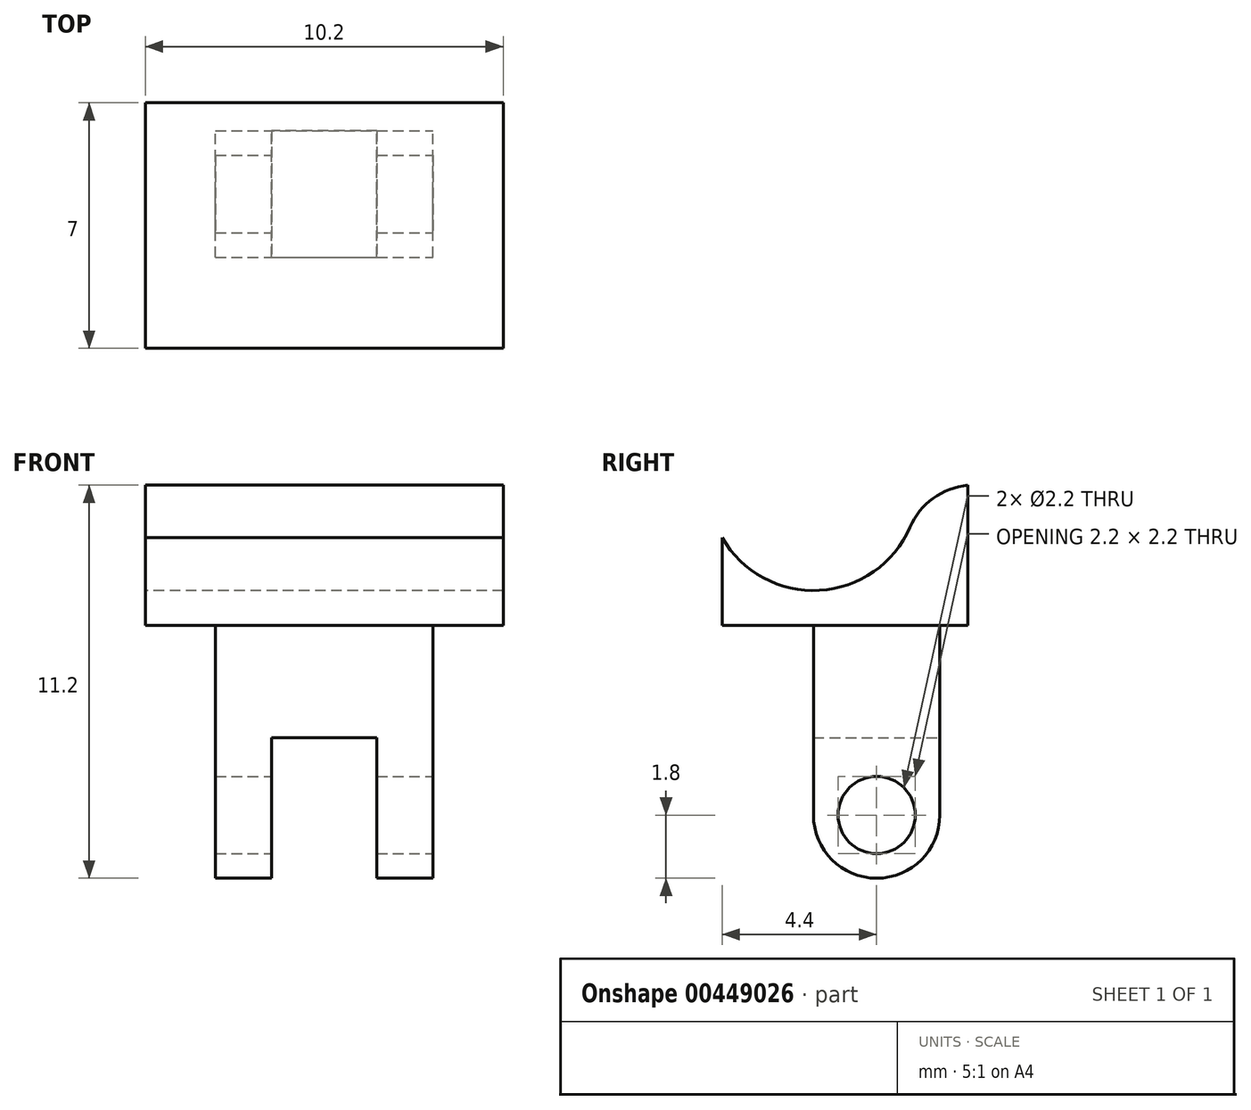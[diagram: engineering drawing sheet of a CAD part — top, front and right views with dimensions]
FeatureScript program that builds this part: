
annotation { "Feature Type Name" : "Feature", "Feature Type Description" : "" }
export const myFeature = defineFeature(function(context is Context, id is Id, definition is map)
    precondition{}
    {
        {
            var Q0;
            Q0=qCreatedBy(makeId("Top.planeOp"),FACE);
            var sketch = newSketch(context, id + "F0", { "sketchPlane" : qUnion([Q0])});
            skLineSegment(sketch, "E0.bottom", {"start": v(0, 0) * mm, "end": v(10.2, 0) * mm});
            skLineSegment(sketch, "E0.top", {"start": v(0, 7) * mm, "end": v(10.2, 7) * mm});
            skLineSegment(sketch, "E0.left", {"start": v(0, 0) * mm, "end": v(0, 7) * mm});
            skLineSegment(sketch, "E0.right", {"start": v(10.2, 0) * mm, "end": v(10.2, 7) * mm});
            skSolve(sketch);
        }
        {
            var Q0;
            Q0 = qSketchRegion(id + "F0", true);
            extrude(context, id + "F1", {"entities" : qUnion([Q0]), "depth" : 4 * mm});
        }
        {
            var Q0;
            Q0=makeQuery(id+"F1.opExtrude","CAP_FACE",FACE,{"disambiguationData":[OSD([sQuery(id+"F0.wireOp",EDGE,"E0.bottom"),sQuery(id+"F0.wireOp",EDGE,"E0.top"),sQuery(id+"F0.wireOp",EDGE,"E0.left"),sQuery(id+"F0.wireOp",EDGE,"E0.right")])],"isStart":true});
            var sketch = newSketch(context, id + "F2", { "sketchPlane" : qUnion([Q0])});
            skLineSegment(sketch, "E1.bottom", {"start": v(2, -2.6) * mm, "end": v(8.2, -2.6) * mm});
            skLineSegment(sketch, "E1.top", {"start": v(2, -6.2) * mm, "end": v(8.2, -6.2) * mm});
            skLineSegment(sketch, "E1.left", {"start": v(2, -2.6) * mm, "end": v(2, -6.2) * mm});
            skLineSegment(sketch, "E1.right", {"start": v(8.2, -2.6) * mm, "end": v(8.2, -6.2) * mm});
            skSolve(sketch);
        }
        {
            var Q0;
            Q0 = qSketchRegion(id + "F2", true);
            extrude(context, id + "F3", {"entities" : qUnion([Q0]), "operationType" : NewBodyOperationType.ADD, "depth" : 7.2 * mm});
        }
        {
            var Q0;
            Q0=makeQuery(id+"F3.opExtrude","SWEPT_FACE",FACE,{"disambiguationData":[OSD([sQuery(id+"F2.wireOp",EDGE,"E1.top")])]});
            var sketch = newSketch(context, id + "F4", { "sketchPlane" : qUnion([Q0])});
            skLineSegment(sketch, "E2.bottom", {"start": v(-6.6, -7.2) * mm, "end": v(-3.6, -7.2) * mm});
            skLineSegment(sketch, "E2.top", {"start": v(-6.6, -3.2) * mm, "end": v(-3.6, -3.2) * mm});
            skLineSegment(sketch, "E2.left", {"start": v(-6.6, -7.2) * mm, "end": v(-6.6, -3.2) * mm});
            skLineSegment(sketch, "E2.right", {"start": v(-3.6, -7.2) * mm, "end": v(-3.6, -3.2) * mm});
            skSolve(sketch);
        }
        {
            var Q0;
            Q0 = qSketchRegion(id + "F4", true);
            extrude(context, id + "F5", {"entities" : qUnion([Q0]), "operationType" : NewBodyOperationType.REMOVE, "oppositeDirection" : true, "depth" : 25 * mm});
        }
        {
            var Q0;
            {var subQ0=sQuery(id+"F2.wireOp",EDGE,"E1.bottom");var subQ1=sQuery(id+"F2.wireOp",EDGE,"E1.left");Q0=makeQuery(id+"F5.boolean.opBoolean","SPLIT",EDGE,{"disambiguationData":[TD([makeQuery(id+"F3.opExtrude","SWEPT_FACE",FACE,{"disambiguationData":[OSD([subQ1])]})])],"derivedFrom":makeQuery(id+"F3.opExtrude","CAP_EDGE",EDGE,{"disambiguationData":[OSD([subQ0])],"isStart":false})});}
            var Q1;
            {var subQ0=sQuery(id+"F2.wireOp",EDGE,"E1.bottom");var subQ1=sQuery(id+"F2.wireOp",EDGE,"E1.right");Q1=makeQuery(id+"F5.boolean.opBoolean","SPLIT",EDGE,{"disambiguationData":[TD([makeQuery(id+"F3.opExtrude","SWEPT_FACE",FACE,{"disambiguationData":[OSD([subQ1])]})])],"derivedFrom":makeQuery(id+"F3.opExtrude","CAP_EDGE",EDGE,{"disambiguationData":[OSD([subQ0])],"isStart":false})});}
            var Q2;
            {var subQ0=sQuery(id+"F2.wireOp",EDGE,"E1.left");var subQ1=sQuery(id+"F2.wireOp",EDGE,"E1.top");Q2=makeQuery(id+"F5.boolean.opBoolean","SPLIT",EDGE,{"disambiguationData":[TD([makeQuery(id+"F3.opExtrude","SWEPT_FACE",FACE,{"disambiguationData":[OSD([subQ0])]})])],"derivedFrom":makeQuery(id+"F3.opExtrude","CAP_EDGE",EDGE,{"disambiguationData":[OSD([subQ1])],"isStart":false})});}
            var Q3;
            {var subQ0=sQuery(id+"F2.wireOp",EDGE,"E1.right");var subQ1=sQuery(id+"F2.wireOp",EDGE,"E1.top");Q3=makeQuery(id+"F5.boolean.opBoolean","SPLIT",EDGE,{"disambiguationData":[TD([makeQuery(id+"F3.opExtrude","SWEPT_FACE",FACE,{"disambiguationData":[OSD([subQ0])]})])],"derivedFrom":makeQuery(id+"F3.opExtrude","CAP_EDGE",EDGE,{"disambiguationData":[OSD([subQ1])],"isStart":false})});}
            fillet(context, id + "F6", {"entities" : qUnion([Q0, Q1, Q2, Q3]), "radius" : 1.8 * mm, "tangentPropagation" : true, "allowEdgeOverflow" : false});
        }
        {
            var Q0;
            Q0=makeQuery(id+"F3.opExtrude","SWEPT_FACE",FACE,{"disambiguationData":[OSD([sQuery(id+"F2.wireOp",EDGE,"E1.right")])]});
            var sketch = newSketch(context, id + "F7", { "sketchPlane" : qUnion([Q0])});
            skCircle(sketch, "E3", {"center": v(4.4, -5.4) * mm, "radius": 1.1 * mm});
            skSolve(sketch);
        }
        {
            var Q0;
            Q0 = qSketchRegion(id + "F7", true);
            extrude(context, id + "F8", {"entities" : qUnion([Q0]), "operationType" : NewBodyOperationType.REMOVE, "oppositeDirection" : true, "depth" : 25 * mm});
        }
        {
            var Q0;
            Q0=makeQuery(id+"F1.opExtrude","SWEPT_FACE",FACE,{"disambiguationData":[OSD([sQuery(id+"F0.wireOp",EDGE,"E0.left")])]});
            var sketch = newSketch(context, id + "F9", { "sketchPlane" : qUnion([Q0])});
            skCircle(sketch, "E4", {"center": v(-2.6, 4) * mm, "radius": 3 * mm});
            skSolve(sketch);
        }
        {
            var Q0;
            Q0 = qSketchRegion(id + "F9", true);
            extrude(context, id + "F10", {"entities" : qUnion([Q0]), "operationType" : NewBodyOperationType.REMOVE, "oppositeDirection" : true, "depth" : 25 * mm});
        }
        {
            var Q0;
            Q0=makeQuery(id+"F10.boolean.opBoolean","INTERSECT",EDGE,{"derivedFrom":[makeQuery(id+"F1.opExtrude","CAP_FACE",FACE,{"disambiguationData":[OSD([sQuery(id+"F0.wireOp",EDGE,"E0.bottom"),sQuery(id+"F0.wireOp",EDGE,"E0.top"),sQuery(id+"F0.wireOp",EDGE,"E0.left"),sQuery(id+"F0.wireOp",EDGE,"E0.right")])],"isStart":false}),makeQuery(id+"F10.opExtrude","SWEPT_FACE",FACE,{"disambiguationData":[OSD([sQuery(id+"F9.wireOp",EDGE,"E4")])]})]});
            fillet(context, id + "F11", {"entities" : qUnion([Q0]), "radius" : 2 * mm, "tangentPropagation" : true, "allowEdgeOverflow" : false});
        }
    });
